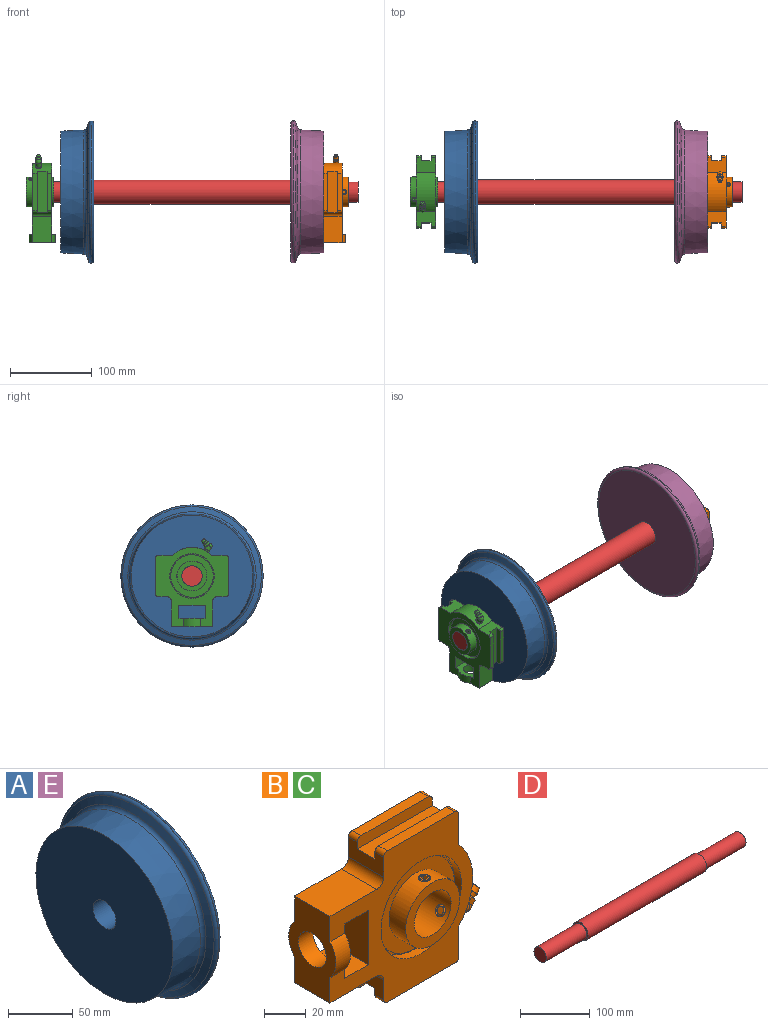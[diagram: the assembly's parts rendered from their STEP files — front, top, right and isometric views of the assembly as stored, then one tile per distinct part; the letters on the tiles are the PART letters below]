
ASSEMBLY  parts=5 mates=4
PART A: 9 faces, bbox 40.5x188.7x188.7 mm
  f0: cone r=74.58mm half-angle=3deg, axis (1,0,0), area 13427mm2, adj f1,f7
  f1: plane 149.16x149.16mm, normal (-1,0,0), area 16986mm2, adj f0,f8
  f2: plane 168x168mm, normal (1,0,0), area 21680.1mm2, adj f3,f8
  f3: torus R=84mm, axis (1,0,0), area 2695.6mm2, adj f2,f4
  f4: cylinder r=87.18mm len=174.35mm, axis (1,0,0), area 72.4mm2, adj f3,f5
  f5: torus R=84mm, axis (1,0,0), area 2106.8mm2, adj f4,f6
  f6: cone r=78.67mm half-angle=70deg, axis (1,0,0), area 3513.4mm2, adj f5,f7
  f7: torus R=80.03mm, axis (1,0,0), area 2245.7mm2, adj f0,f6
  f8: cylinder r=12.45mm len=40.48mm, axis (1,0,0), area 3166.7mm2, adj f1,f2
PART B: 128 faces, bbox 108.9x37.1x90.3 mm
  f0: sphere r=0.63mm, area 0.7mm2, adj f1
  f1: plane 4.68x3.6mm, normal (0.77,0,0.64), area 16.1mm2, adj f0,f2
  f2: cone r=1.7mm half-angle=15deg, axis (-0.77,0,-0.64), area 55.9mm2, adj f1,f3
  f3: cone r=3.7mm half-angle=10deg, axis (0.77,0,0.64), area 42.4mm2, adj f2,f4
  f4: cone r=0mm half-angle=60deg, axis (-0.77,0,-0.64), area 31.8mm2, adj f3,f5,f123,f124,f125,f126,f127
  f5: plane 5.98x5.8mm, normal (0,-1,0), area 11.9mm2, adj f4,f6,f122,f123,f127
  f6: cone r=6.09mm half-angle=60deg, axis (0.77,0,0.64), area 1.2mm2, adj f5,f7,f121,f127
  f7: plane 5.61x1.62mm, normal (0.77,0,0.64), area 3.2mm2, adj f6,f8,f119,f120
  f8: cone r=6.09mm half-angle=60deg, axis (0.77,0,0.64), area 1.2mm2, adj f7,f9,f125,f126
  f9: plane 4.32x3.64mm, normal (-0.77,0,-0.64), area 3.4mm2, adj f8,f10,f12,f13,f118,f119
  f10: cone r=4.59mm half-angle=60deg, axis (0.77,0,0.64), area 0.8mm2, adj f9,f11,f121,f123,f124
  f11: plane 1.43x0.17mm, normal (0.77,0,0.64), area 0.1mm2, adj f10,f13
  f12: cylinder r=2.8mm len=1.89mm, axis (-0.77,0,-0.64), area 0mm2, adj f9,f13
  f13: cylinder r=3.5mm len=8.63mm, axis (-0.87,0,0.5), area 94.5mm2, adj f9,f11,f12,f14,f112,f113,f114,f115
  f14: cone r=2.19mm half-angle=60deg, axis (-0.87,0,0.5), area 1.2mm2, adj f13,f15,f111
  f15: plane 4.13x3.41mm, normal (-0.25,0.87,-0.43), area 7.9mm2, adj f14,f16,f109,f110,f111,f117
  f16: cone r=4.95mm half-angle=60deg, axis (0.87,0,-0.5), area 1.2mm2, adj f15,f17,f111
  f17: plane 7.05x6.07mm, normal (-0.87,0,0.5), area 10.2mm2, adj f16,f18,f22,f23,f24,f25,f110
  f18: cone r=4.95mm half-angle=60deg, axis (0.87,0,-0.5), area 1.2mm2, adj f17,f19,f111
  f19: plane 4.13x3.41mm, normal (-0.25,-0.87,-0.43), area 7.9mm2, adj f18,f20,f24,f111,f112,f113
  f20: plane 4.13x3.41mm, normal (0.25,-0.87,0.43), area 7.9mm2, adj f19,f21,f23,f24,f113,f114
  f21: plane 4.37x2.2mm, normal (0.5,0,0.87), area 7.9mm2, adj f20,f22,f23,f109,f114,f115
  f22: cone r=5.22mm half-angle=60deg, axis (0.87,0,-0.5), area 1.2mm2, adj f17,f21,f109
  f23: cone r=5.22mm half-angle=60deg, axis (0.87,0,-0.5), area 1.2mm2, adj f17,f20,f21
  f24: cone r=5.54mm half-angle=60deg, axis (0.87,0,-0.5), area 1mm2, adj f17,f19,f20
  f25: cylinder r=3mm len=6mm, axis (-0.87,0,0.5), area 1.4mm2, adj f17,f26
  f26: cylinder r=35mm len=47.95mm, axis (0,-1,0), area 1244.5mm2, adj f25,f27,f106,f107,f108
  f27: plane 97.8x89.8mm, normal (0,1,0), area 3653.9mm2, adj f26,f28,f74,f75,f76,f77,f84,f85
  f28: cylinder r=27.3mm len=54.6mm, axis (0,-1,0), area 823.3mm2, adj f27,f29
  f29: plane 55.36x55.36mm, normal (0,1,0), area 219mm2, adj f28,f30
  f30: cylinder r=26mm len=52mm, axis (0,-1,0), area 212.4mm2, adj f29,f31
  f31: plane 52.54x52.54mm, normal (0,1,0), area 1063.9mm2, adj f30,f32
  f32: cylinder r=18.37mm len=36.75mm, axis (0,-1,0), area 669.5mm2, adj f31,f33
  f33: plane 37.11x37.11mm, normal (0,1,0), area 569.9mm2, adj f32,f34
  f34: cylinder r=12.5mm len=34.1mm, axis (0,-1,0), area 2625.6mm2, adj f33,f35,f38,f41,f42
  f35: cylinder r=3mm len=6mm, axis (0.87,0,-0.5), area 23.9mm2, adj f34,f36
  f36: cone r=0.08mm half-angle=45deg, axis (0.87,0,-0.5), area 22.2mm2, adj f35,f37
  f37: plane 4.06x3.52mm, normal (-0.87,0,0.5), area 12.6mm2, adj f36
  f38: cylinder r=3mm len=5.4mm, axis (0,0,1), area 10.5mm2, adj f34,f39,f41
  f39: cone r=2mm half-angle=45deg, axis (0,0,1), area 22.2mm2, adj f38,f40,f41
  f40: plane 4.06x4.06mm, normal (0,0,-1), area 12.6mm2, adj f39
  f41: cylinder r=3mm len=5.4mm, axis (0,0,1), area 11.2mm2, adj f34,f38,f39
  f42: plane 37.11x37.11mm, normal (0,-1,0), area 569.9mm2, adj f34,f43
  f43: cylinder r=18.37mm len=36.75mm, axis (0,-1,0), area 1249.1mm2, adj f42,f44,f45,f54,f55,f56,f57,f58
  f44: cylinder r=3mm len=0.85mm, axis (-0.87,0,0.5), area 0mm2, adj f43,f45
  f45: cone r=0mm half-angle=60deg, axis (-0.87,0,0.5), area 12mm2, adj f43,f44,f46,f54,f55,f56
  f46: plane 4.84x4.2mm, normal (0.87,0,-0.5), area 10.1mm2, adj f45,f47,f49,f50,f51,f52,f53
  f47: plane 3.03x2.25mm, normal (-0.43,-0.5,-0.75), area 5.2mm2, adj f46,f48,f49,f53
  f48: plane 3x3mm, normal (0.87,0,-0.5), area 7.8mm2, adj f47,f49,f50,f51,f52,f53
  f49: plane 3.03x2.25mm, normal (-0.43,0.5,-0.75), area 5.2mm2, adj f46,f47,f48,f50
  f50: plane 3.46x3mm, normal (0,1,0), area 5.2mm2, adj f46,f48,f49,f51
  f51: plane 3.03x2.25mm, normal (0.43,0.5,0.75), area 5.2mm2, adj f46,f48,f50,f52
  f52: plane 3.03x2.25mm, normal (0.43,-0.5,0.75), area 5.2mm2, adj f46,f48,f51,f53
  f53: plane 3.46x3mm, normal (0,-1,0), area 5.2mm2, adj f46,f47,f48,f52
  f54: cylinder r=3mm len=5.02mm, axis (0.87,0,-0.5), area 0.3mm2, adj f43,f45
  f55: cylinder r=3mm len=1.7mm, axis (-0.87,0,0.5), area 0mm2, adj f43,f45
  f56: cylinder r=3mm len=5.02mm, axis (0.87,0,-0.5), area 0.3mm2, adj f43,f45
  f57: cylinder r=3mm len=0.85mm, axis (0,0,-1), area 0mm2, adj f43,f58
  f58: cone r=2.39mm half-angle=60deg, axis (0,0,-1), area 12mm2, adj f43,f57,f59,f67,f68,f69
  f59: plane 4.84x4.84mm, normal (0,0,1), area 10.1mm2, adj f58,f60,f62,f63,f64,f65,f66
  f60: plane 3x1.5mm, normal (0.87,-0.5,0), area 5.2mm2, adj f59,f61,f62,f66
  f61: plane 3.46x3mm, normal (0,0,1), area 7.8mm2, adj f60,f62,f63,f64,f65,f66
  f62: plane 3x1.5mm, normal (0.87,0.5,0), area 5.2mm2, adj f59,f60,f61,f63
  f63: plane 3x1.73mm, normal (0,1,0), area 5.2mm2, adj f59,f61,f62,f64
  f64: plane 3x1.5mm, normal (-0.87,0.5,0), area 5.2mm2, adj f59,f61,f63,f65
  f65: plane 3x1.5mm, normal (-0.87,-0.5,0), area 5.2mm2, adj f59,f61,f64,f66
  f66: plane 3x1.73mm, normal (0,-1,0), area 5.2mm2, adj f59,f60,f61,f65
  f67: cylinder r=3mm len=5.75mm, axis (0,0,1), area 0.9mm2, adj f43,f58
  f68: cylinder r=3mm len=1.7mm, axis (0,0,-1), area 0mm2, adj f43,f58
  f69: cylinder r=3mm len=5.75mm, axis (0,0,1), area 0.9mm2, adj f43,f58
  f70: plane 52.54x52.54mm, normal (0,-1,0), area 1063.9mm2, adj f43,f71
  f71: cylinder r=26mm len=52mm, axis (0,-1,0), area 212.4mm2, adj f70,f72
  f72: plane 55.36x55.36mm, normal (0,-1,0), area 219mm2, adj f71,f73
  f73: cylinder r=27.3mm len=54.6mm, axis (0,1,0), area 823.3mm2, adj f72,f107
  f74: plane 24x16mm, normal (0,0,1), area 384mm2, adj f27,f103,f105,f107
  f75: plane 31.75x24mm, normal (0,0,-1), area 762mm2, adj f27,f76,f99,f107
  f76: cylinder r=4.75mm len=24mm, axis (0,-1,0), area 179.1mm2, adj f27,f75,f77,f107
  f77: plane 24x11.7mm, normal (-1,0,0), area 233.4mm2, adj f27,f76,f78,f81,f82,f83,f84,f107
  f78: cylinder r=2.55mm len=6mm, axis (0,1,0), area 24mm2, adj f77,f79,f81,f107
  f79: plane 45.9x6mm, normal (0,0,-1), area 275.4mm2, adj f78,f80,f81,f107
  f80: cylinder r=2.55mm len=6mm, axis (0,1,0), area 24mm2, adj f79,f81,f106,f107
  f81: plane 51.16x6.66mm, normal (0,1,0), area 328.7mm2, adj f77,f78,f79,f80,f82,f106
  f82: plane 51x12mm, normal (0,0,-1), area 612mm2, adj f77,f81,f83,f106
  f83: plane 51.16x6.66mm, normal (0,-1,0), area 328.7mm2, adj f77,f82,f84,f85,f86,f106
  f84: cylinder r=2.55mm len=6mm, axis (0,1,0), area 24mm2, adj f27,f77,f83,f85
  f85: plane 45.9x6mm, normal (0,0,-1), area 275.4mm2, adj f27,f83,f84,f86
  f86: cylinder r=2.55mm len=6mm, axis (0,1,0), area 24mm2, adj f27,f83,f85,f106
  f87: cylinder r=2.55mm len=6mm, axis (0,1,0), area 24mm2, adj f27,f88,f94,f108
  f88: plane 51.16x6.66mm, normal (0,-1,0), area 328.7mm2, adj f87,f89,f94,f95,f96,f108
  f89: plane 51x12mm, normal (0,0,1), area 612mm2, adj f88,f90,f96,f108
  f90: plane 51.16x6.66mm, normal (0,1,0), area 328.7mm2, adj f89,f91,f92,f93,f96,f108
  f91: cylinder r=2.55mm len=6mm, axis (0,1,0), area 24mm2, adj f90,f92,f107,f108
  f92: plane 45.9x6mm, normal (0,0,1), area 275.4mm2, adj f90,f91,f93,f107
  f93: cylinder r=2.55mm len=6mm, axis (0,1,0), area 24mm2, adj f90,f92,f96,f107
  f94: plane 45.9x6mm, normal (0,0,1), area 275.4mm2, adj f27,f87,f88,f95
  f95: cylinder r=2.55mm len=6mm, axis (0,1,0), area 24mm2, adj f27,f88,f94,f96
  f96: plane 24x11.7mm, normal (-1,0,0), area 233.4mm2, adj f27,f88,f89,f90,f93,f95,f97,f107
  f97: cylinder r=4.75mm len=24mm, axis (0,1,0), area 179.1mm2, adj f27,f96,f98,f107
  f98: plane 31.75x24mm, normal (0,0,1), area 762mm2, adj f27,f97,f99,f107
  f99: plane 51.98x33.01mm, normal (-1,0,0), area 1056.6mm2, adj f27,f75,f98,f100,f101,f102,f107
  f100: cylinder r=9.5mm len=19mm, axis (1,0,0), area 596.9mm2, adj f99,f103
  f101: cylinder r=16mm len=21.17mm, axis (-1,0,0), area 231.3mm2, adj f99,f103,f107
  f102: cylinder r=16mm len=21.17mm, axis (-1,0,0), area 231.3mm2, adj f27,f99,f103
  f103: plane 32x32mm, normal (1,0,0), area 600.5mm2, adj f27,f74,f100,f101,f102,f104,f107
  f104: plane 24x16mm, normal (0,0,-1), area 384mm2, adj f27,f103,f105,f107
  f105: plane 32x24mm, normal (-1,0,0), area 768mm2, adj f27,f74,f104,f107
  f106: plane 24x17.98mm, normal (1,0,0), area 384mm2, adj f26,f27,f80,f81,f82,f83,f86,f107
  f107: plane 97.8x89.8mm, normal (0,-1,0), area 3653.9mm2, adj f26,f73,f74,f75,f76,f77,f78,f79
  f108: plane 24x17.98mm, normal (1,0,0), area 384mm2, adj f26,f27,f87,f88,f89,f90,f91,f107
  f109: plane 4.13x3.41mm, normal (0.25,0.87,0.43), area 7.9mm2, adj f15,f21,f22,f110,f115,f117
  f110: cone r=5.61mm half-angle=60deg, axis (0.87,0,-0.5), area 1mm2, adj f15,f17,f109
  f111: plane 4.37x2.2mm, normal (-0.5,0,-0.87), area 7.9mm2, adj f14,f15,f16,f18,f19,f112
  f112: cone r=2.19mm half-angle=60deg, axis (-0.87,0,0.5), area 1.2mm2, adj f13,f19,f111
  f113: cone r=1.51mm half-angle=60deg, axis (-0.87,0,0.5), area 1mm2, adj f13,f19,f20
  f114: cone r=2.19mm half-angle=60deg, axis (-0.87,0,0.5), area 1.2mm2, adj f13,f20,f21
  f115: cone r=2.19mm half-angle=60deg, axis (-0.87,0,0.5), area 1.2mm2, adj f13,f21,f109
  f116: cylinder r=2.8mm len=1.89mm, axis (-0.77,0,-0.64), area 0mm2, adj f13,f121
  f117: cone r=1.51mm half-angle=60deg, axis (-0.87,0,0.5), area 1mm2, adj f13,f15,f109
  f118: cone r=6.09mm half-angle=60deg, axis (0.77,0,0.64), area 1.2mm2, adj f9,f124,f125
  f119: sphere r=3.5mm, area 52.8mm2, adj f7,f9,f13,f121
  f120: cone r=4.68mm half-angle=60deg, axis (0.77,0,0.64), area 1mm2, adj f7,f126,f127
  f121: plane 4.32x3.64mm, normal (-0.77,0,-0.64), area 3.4mm2, adj f6,f10,f13,f116,f119,f122
  f122: cone r=6.09mm half-angle=60deg, axis (0.77,0,0.64), area 1.2mm2, adj f5,f121,f123
  f123: plane 4.75x4.5mm, normal (-0.56,-0.5,0.66), area 11.9mm2, adj f4,f5,f10,f122,f124
  f124: plane 4.75x4.5mm, normal (-0.56,0.5,0.66), area 11.9mm2, adj f4,f10,f118,f123,f125
  f125: plane 5.98x5.8mm, normal (0,1,0), area 11.9mm2, adj f4,f8,f118,f124,f126
  f126: plane 4.75x4.5mm, normal (0.56,0.5,-0.66), area 11.9mm2, adj f4,f8,f120,f125,f127
  f127: plane 4.75x4.5mm, normal (0.56,-0.5,-0.66), area 11.9mm2, adj f4,f5,f6,f120,f126
PART C: same geometry as B
PART D: 7 faces, bbox 406.4x30x30 mm
  f0: cylinder r=15mm len=241.3mm, axis (-1,0,0), area 22742mm2, adj f1,f2
  f1: plane 30x30mm, normal (1,0,0), area 216mm2, adj f0,f3
  f2: plane 30x30mm, normal (-1,0,0), area 216mm2, adj f0,f5
  f3: cylinder r=12.5mm len=82.55mm, axis (-1,0,0), area 6483.5mm2, adj f1,f4
  f4: plane 25x25mm, normal (1,0,0), area 490.9mm2, adj f3
  f5: cylinder r=12.5mm len=82.55mm, axis (1,0,0), area 6483.5mm2, adj f2,f6
  f6: plane 25x25mm, normal (-1,0,0), area 490.9mm2, adj f5
PART E: same geometry as A
PLACE A t=(-108.17,106.83,15.55)mm
PLACE B rot(axis=(0.58,-0.58,0.58),120deg) t=(224.7,106.83,-46.45)mm
PLACE C rot(axis=(-0.58,-0.58,-0.58),120deg) t=(-130.91,106.83,-46.45)mm
PLACE D t=(-67.69,106.83,15.55)mm
PLACE E rot(axis=(0,1,0),180deg) t=(214.09,106.83,15.55)mm
MATE fastened A.f8 <-> D.f3  axis (1,0,0) through (-67.69,106.83,15.55)mm
MATE cylindrical C.f34 <-> D.f3  axis (-1,0,0) through (-133.66,106.83,15.55)mm
MATE fastened E.f0 <-> D.f3  axis (-1,0,0) through (173.61,106.83,15.55)mm
MATE cylindrical B.f34 <-> D.f3  axis (1,0,0) through (244.5,106.83,15.55)mm
